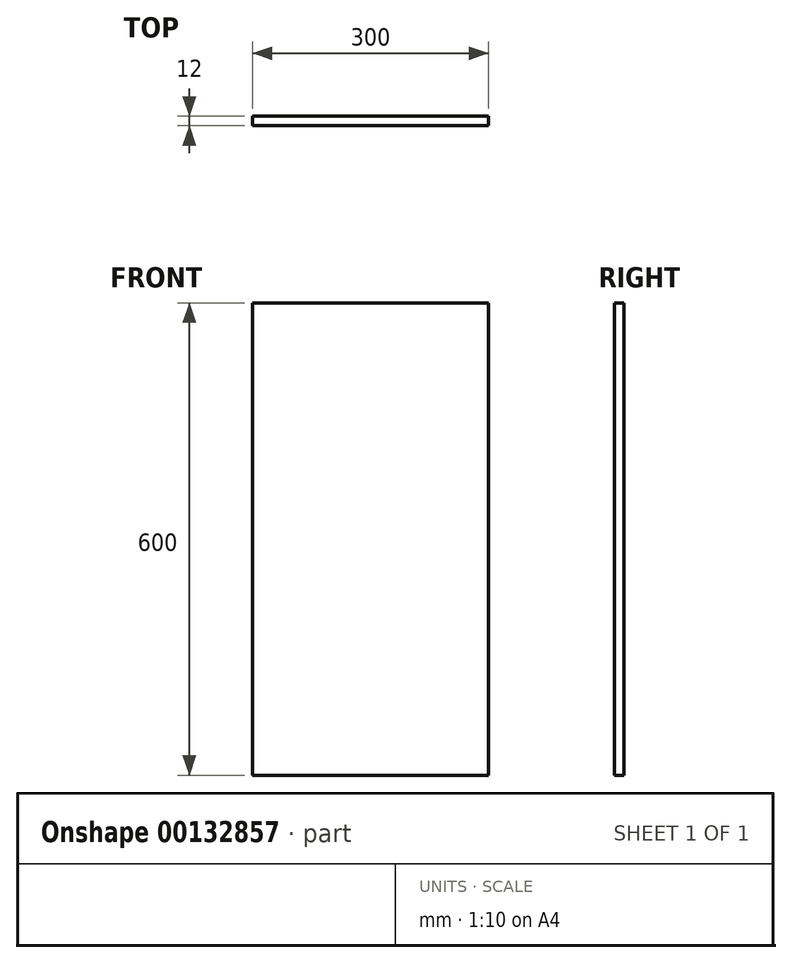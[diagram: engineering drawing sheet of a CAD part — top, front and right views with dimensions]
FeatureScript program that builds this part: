
annotation { "Feature Type Name" : "Feature", "Feature Type Description" : "" }
export const myFeature = defineFeature(function(context is Context, id is Id, definition is map)
    precondition{}
    {
        {
            var Q0;
            Q0=qCreatedBy(makeId("Front.planeOp"),FACE);
            var sketch = newSketch(context, id + "F0", { "sketchPlane" : qUnion([Q0])});
            skLineSegment(sketch, "E0.bottom", {"start": v(0, 0) * mm, "end": v(300, 0) * mm});
            skLineSegment(sketch, "E0.top", {"start": v(0, 600) * mm, "end": v(300, 600) * mm});
            skLineSegment(sketch, "E0.left", {"start": v(0, 0) * mm, "end": v(0, 600) * mm});
            skLineSegment(sketch, "E0.right", {"start": v(300, 0) * mm, "end": v(300, 600) * mm});
            skSolve(sketch);
        }
        {
            var Q0;
            Q0=makeQuery(id+"F0.imprint","IMPRINT",FACE,{"disambiguationData":[TD([[makeQuery(id+"F0.imprint","IMPRINT",EDGE,{"derivedFrom":sQuery(id+"F0.wireOp",EDGE,"E0.bottom")}),1.0]])]});
            extrude(context, id + "F1", {"entities" : qUnion([Q0]), "depth" : 12 * mm});
        }
    });
